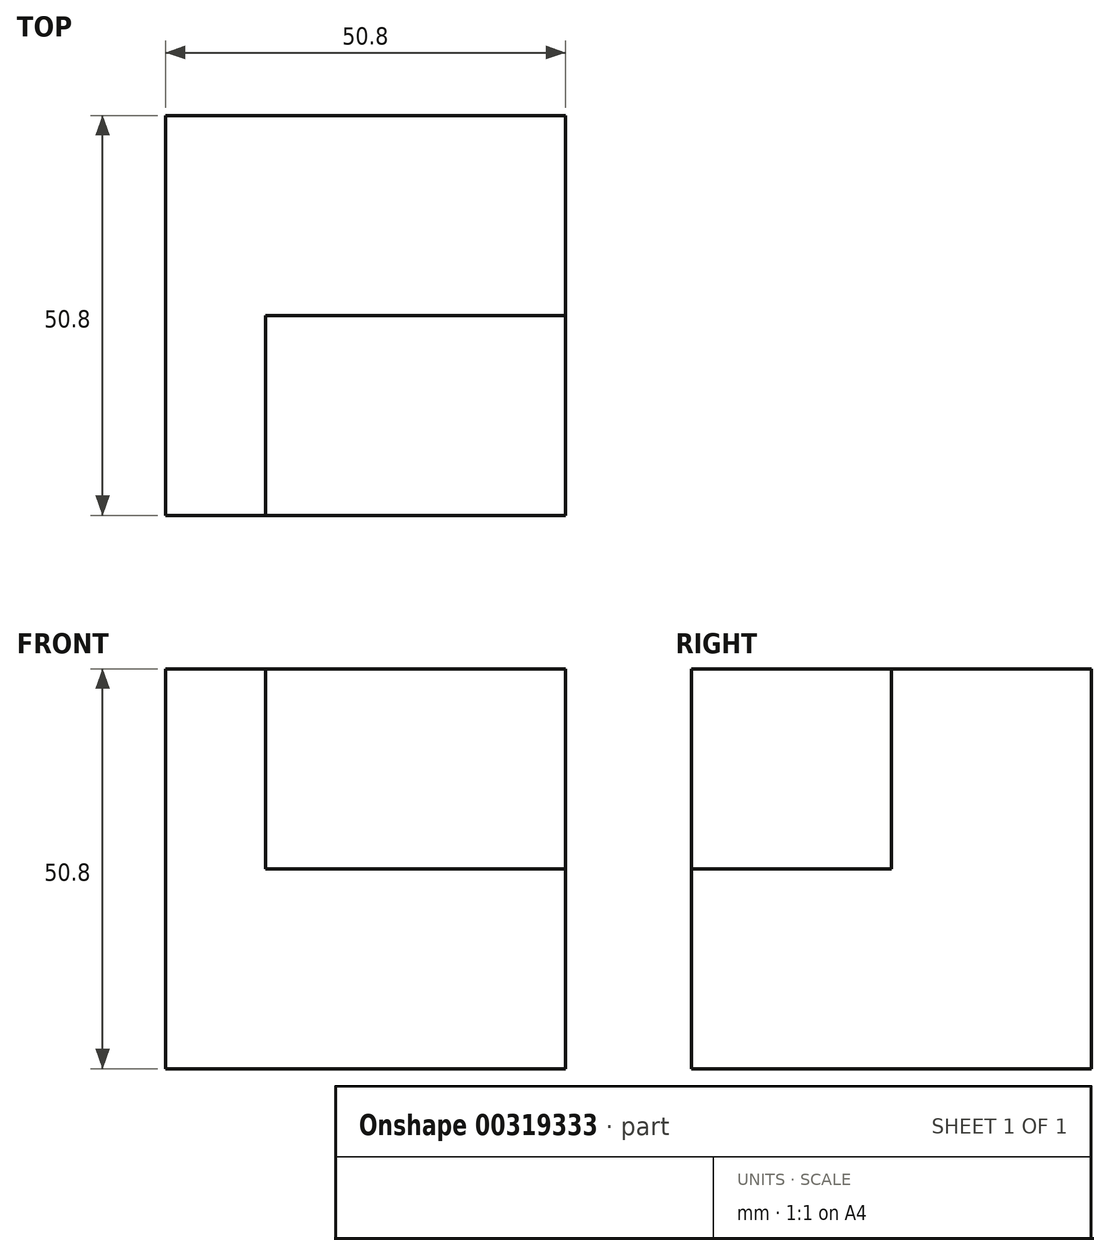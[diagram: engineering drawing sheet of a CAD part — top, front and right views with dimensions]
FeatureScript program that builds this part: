
annotation { "Feature Type Name" : "Feature", "Feature Type Description" : "" }
export const myFeature = defineFeature(function(context is Context, id is Id, definition is map)
    precondition{}
    {
        {
            var Q0;
            Q0=qCreatedBy(makeId("Top.planeOp"),FACE);
            var sketch = newSketch(context, id + "F0", { "sketchPlane" : qUnion([Q0])});
            skLineSegment(sketch, "E0.bottom", {"start": v(-25.16, 24.85) * mm, "end": v(25.64, 24.85) * mm});
            skLineSegment(sketch, "E0.top", {"start": v(-25.16, -25.95) * mm, "end": v(25.64, -25.95) * mm});
            skLineSegment(sketch, "E0.left", {"start": v(-25.16, 24.85) * mm, "end": v(-25.16, -25.95) * mm});
            skLineSegment(sketch, "E0.right", {"start": v(25.64, 24.85) * mm, "end": v(25.64, -25.95) * mm});
            skSolve(sketch);
        }
        {
            var Q0;
            Q0 = qSketchRegion(id + "F0", true);
            extrude(context, id + "F1", {"entities" : qUnion([Q0]), "depth" : 25.4 * mm});
        }
        {
            var Q0;
            Q0=makeQuery(id+"F1.opExtrude","CAP_FACE",FACE,{"disambiguationData":[OSD([sQuery(id+"F0.wireOp",EDGE,"E0.bottom"),sQuery(id+"F0.wireOp",EDGE,"E0.top"),sQuery(id+"F0.wireOp",EDGE,"E0.left"),sQuery(id+"F0.wireOp",EDGE,"E0.right")])],"isStart":false});
            var sketch = newSketch(context, id + "F2", { "sketchPlane" : qUnion([Q0])});
            skLineSegment(sketch, "E1", {"start": v(-25.16, -25.95) * mm, "end": v(-12.46, -25.95) * mm});
            skLineSegment(sketch, "E2", {"start": v(-12.46, -25.95) * mm, "end": v(-12.46, -0.55) * mm});
            skLineSegment(sketch, "E3", {"start": v(-12.46, -0.55) * mm, "end": v(25.64, -0.55) * mm});
            skLineSegment(sketch, "E4", {"start": v(25.64, -0.55) * mm, "end": v(25.64, 24.85) * mm});
            skLineSegment(sketch, "E5", {"start": v(25.64, 24.85) * mm, "end": v(-25.16, 24.85) * mm});
            skLineSegment(sketch, "E6", {"start": v(-25.16, 24.85) * mm, "end": v(-25.16, -25.95) * mm});
            skSolve(sketch);
        }
        {
            var Q0;
            Q0 = qSketchRegion(id + "F2", true);
            extrude(context, id + "F3", {"entities" : qUnion([Q0]), "operationType" : NewBodyOperationType.ADD, "depth" : 25.4 * mm});
        }
    });
